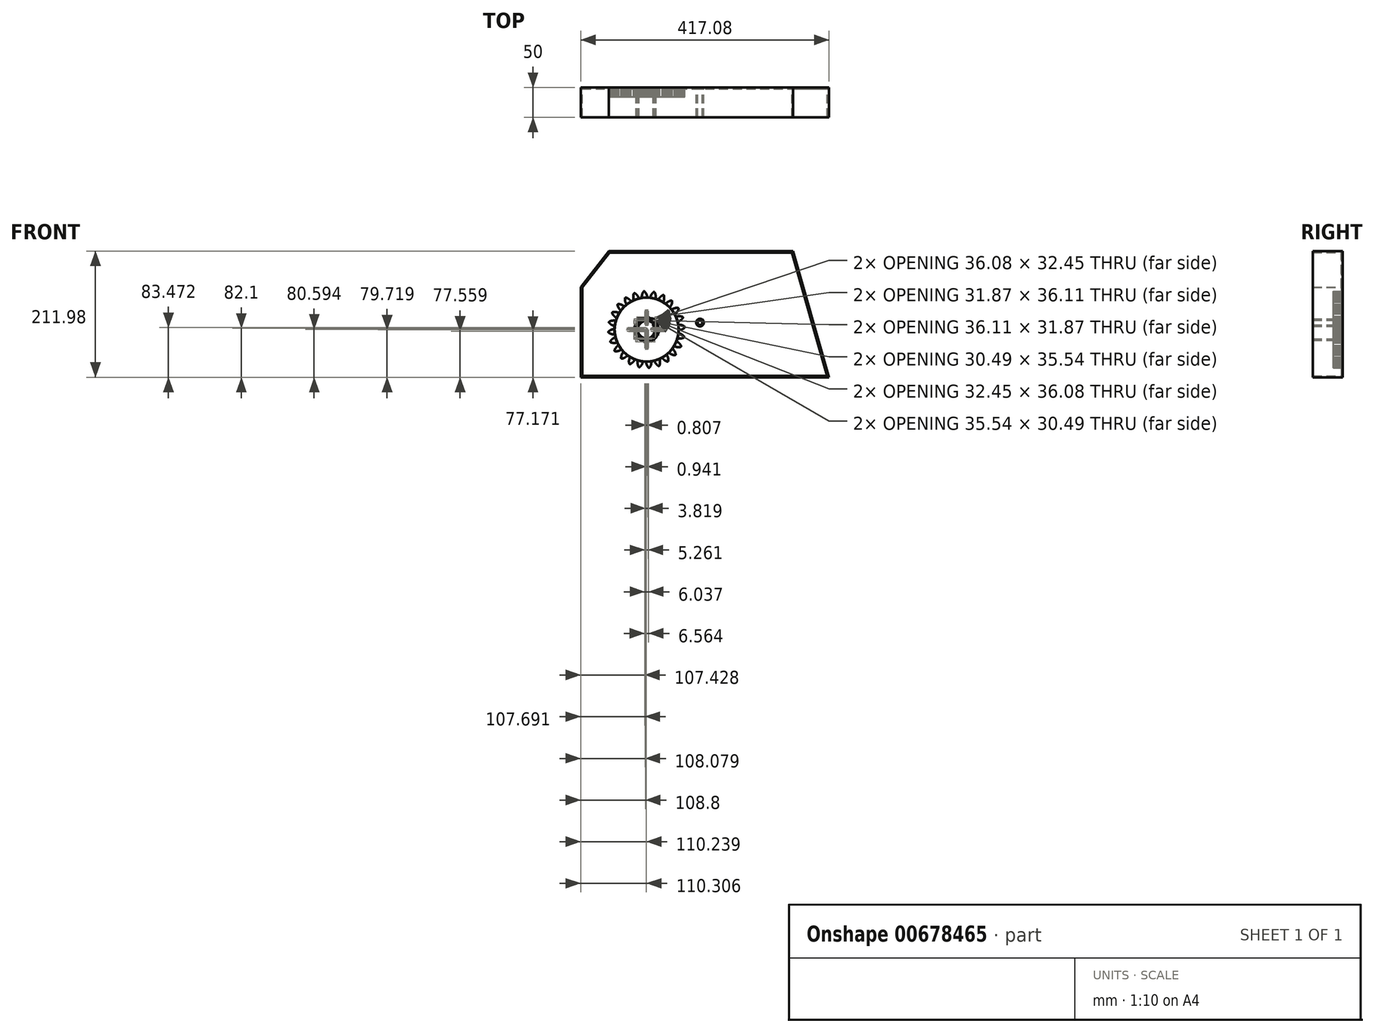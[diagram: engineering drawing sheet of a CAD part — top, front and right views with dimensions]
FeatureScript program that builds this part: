
annotation { "Feature Type Name" : "Feature", "Feature Type Description" : "" }
export const myFeature = defineFeature(function(context is Context, id is Id, definition is map)
    precondition{}
    {
        {
            var Q0;
            Q0=qCreatedBy(makeId("Front.planeOp"),FACE);
            var sketch = newSketch(context, id + "F0", { "sketchPlane" : qUnion([Q0])});
            skCircle(sketch, "E0", {"center": v(0, 0) * mm, "radius": 53.72 * mm});
            skCircle(sketch, "E1", {"center": v(0, 0) * mm, "radius": 58.67 * mm, "construction": true});
            skCircle(sketch, "E2", {"center": v(0, 0) * mm, "radius": 63.5 * mm, "construction": true});
            skLineSegment(sketch, "E3", {"start": v(0, 0) * mm, "end": v(0, 95.37) * mm, "construction": true});
            skLineSegment(sketch, "E4", {"start": v(0, 0) * mm, "end": v(-6.26, 95.47) * mm, "construction": true});
            skLineSegment(sketch, "E5", {"start": v(0, 58.67) * mm, "end": v(-48.27, 58.67) * mm, "construction": true});
            skLineSegment(sketch, "E6", {"start": v(0, 58.67) * mm, "end": v(-46.06, 41.9) * mm, "construction": true});
            skCircle(sketch, "E7", {"center": v(0, 0) * mm, "radius": 55.14 * mm, "construction": true});
            skCircle(sketch, "E8", {"center": v(0, 58.67) * mm, "radius": 14.6 * mm, "construction": true});
            skCircle(sketch, "E9", {"center": v(-13.72, 53.68) * mm, "radius": 14.6 * mm, "construction": true});
            skArc(sketch, "E10", {"start": v(0, 58.67) * mm, "mid": v(-1.2, 61.2) * mm, "end": v(-2.86, 63.44) * mm});
            skArc(sketch, "E11", {"start": v(0.88, 53.71) * mm, "mid": v(0.65, 56.23) * mm, "end": v(0, 58.67) * mm});
            skArc(sketch, "E12.MirrorCS", {"start": v(-7.66, 58.17) * mm, "mid": v(-6.8, 60.83) * mm, "end": v(-5.45, 63.27) * mm});
            skArc(sketch, "E13.MirrorCS", {"start": v(-7.88, 53.14) * mm, "mid": v(-7.98, 55.67) * mm, "end": v(-7.66, 58.17) * mm});
            skArc(sketch, "E14", {"start": v(-2.86, 63.44) * mm, "mid": v(-4.21, 64.26) * mm, "end": v(-5.45, 63.27) * mm});
            skCircle(sketch, "E15", {"center": v(0.45, 0.15) * mm, "radius": 15.34 * mm});
            skLineSegment(sketch, "E16", {"start": v(-7.74, 13.12) * mm, "end": v(-7.74, 19.4) * mm});
            skLineSegment(sketch, "E17", {"start": v(10.07, 12.1) * mm, "end": v(10.07, 18.83) * mm});
            skLineSegment(sketch, "E18", {"start": v(-7.74, 19.4) * mm, "end": v(10.07, 18.83) * mm});
            skSolve(sketch);
        }
        {
            var Q0;
            Q0=makeQuery(id+"F0.imprint","IMPRINT",FACE,{"disambiguationData":[TD([[makeQuery(id+"F0.imprint","IMPRINT",EDGE,{"derivedFrom":sQuery(id+"F0.wireOp",EDGE,"E10")}),1.0]])]});
            var Q1;
            {var subQ0=sQuery(id+"F0.wireOp",EDGE,"E0");var subQ1=makeQuery(id+"F0.imprint","INTERSECT",VERTEX,{"derivedFrom":[subQ0,sQuery(id+"F0.wireOp",EDGE,"E11")]});Q1=makeQuery(id+"F0.imprint","IMPRINT",FACE,{"disambiguationData":[TD([[makeQuery(id+"F0.imprint","IMPRINT",EDGE,{"disambiguationData":[TD([[subQ1,-1.0]])],"derivedFrom":subQ0}),1.0]])]});}
            extrude(context, id + "F1", {"entities" : qUnion([Q0, Q1]), "depth" : 16 * mm, "offsetDistance" : 25 * mm});
        }
        {
            var Q0;
            Q0=makeQuery(id+"F1.opExtrude","SWEPT_BODY",BODY,{"disambiguationData":[OSD([sQuery(id+"F0.wireOp",EDGE,"E0"),sQuery(id+"F0.wireOp",EDGE,"E10"),sQuery(id+"F0.wireOp",EDGE,"E11"),sQuery(id+"F0.wireOp",EDGE,"E12.MirrorCS"),sQuery(id+"F0.wireOp",EDGE,"E13.MirrorCS"),sQuery(id+"F0.wireOp",EDGE,"E14")])]});
            var Q1;
            Q1=makeQuery(id+"F1.opExtrude","SWEPT_FACE",FACE,{"disambiguationData":[OSD([sQuery(id+"F0.wireOp",EDGE,"E0")])]});
            circularPattern(context, id + "F2", {"entities" : qUnion([Q0]), "axis" : qUnion([Q1]), "angle" : 360 * degree, "instanceCount" : 24, "equalSpace" : true});
        }
        {
            var Q0;
            Q0=qCreatedBy(makeId("Front.planeOp"),FACE);
            var sketch = newSketch(context, id + "F3", { "sketchPlane" : qUnion([Q0])});
            skLineSegment(sketch, "E19", {"start": v(-110.71, 71.74) * mm, "end": v(-110.71, -80.19) * mm});
            skLineSegment(sketch, "E20", {"start": v(-110.71, -80.19) * mm, "end": v(306.37, -80.19) * mm});
            skLineSegment(sketch, "E21", {"start": v(-110.71, 71.74) * mm, "end": v(-63.68, 131.79) * mm});
            skLineSegment(sketch, "E22", {"start": v(-63.68, 131.79) * mm, "end": v(245.7, 131.79) * mm});
            skLineSegment(sketch, "E23", {"start": v(245.7, 131.79) * mm, "end": v(306.37, -80.19) * mm});
            skCircle(sketch, "E24", {"center": v(-0.93, -1.23) * mm, "radius": 14.2 * mm});
            skLineSegment(sketch, "E25", {"start": v(-12.6, 6.84) * mm, "end": v(-12.6, 15.4) * mm});
            skLineSegment(sketch, "E26", {"start": v(-12.6, 15.4) * mm, "end": v(10.72, 15.4) * mm});
            skLineSegment(sketch, "E27", {"start": v(10.72, 15.4) * mm, "end": v(10.72, 6.89) * mm});
            skCircle(sketch, "E28", {"center": v(89.67, 11.82) * mm, "radius": 3.94 * mm});
            skSolve(sketch);
        }
        {
            var Q0;
            Q0=makeQuery(id+"F3.imprint","IMPRINT",FACE,{"disambiguationData":[TD([[makeQuery(id+"F3.imprint","IMPRINT",EDGE,{"derivedFrom":sQuery(id+"F3.wireOp",EDGE,"E19")}),1.0]])]});
            extrude(context, id + "F4", {"entities" : qUnion([Q0]), "depth" : 50 * mm, "offsetDistance" : 25 * mm});
        }
        {
            var Q0;
            Q0=makeQuery(id+"F4.opExtrude","CAP_FACE",FACE,{"disambiguationData":[OSD([sQuery(id+"F3.wireOp",EDGE,"E19"),sQuery(id+"F3.wireOp",EDGE,"E20"),sQuery(id+"F3.wireOp",EDGE,"E21"),sQuery(id+"F3.wireOp",EDGE,"E22"),sQuery(id+"F3.wireOp",EDGE,"E23")])],"isStart":false});
            shell(context, id + "F5", {"entities" : qUnion([Q0]), "thickness" : 2.5 * mm});
        }
    });
